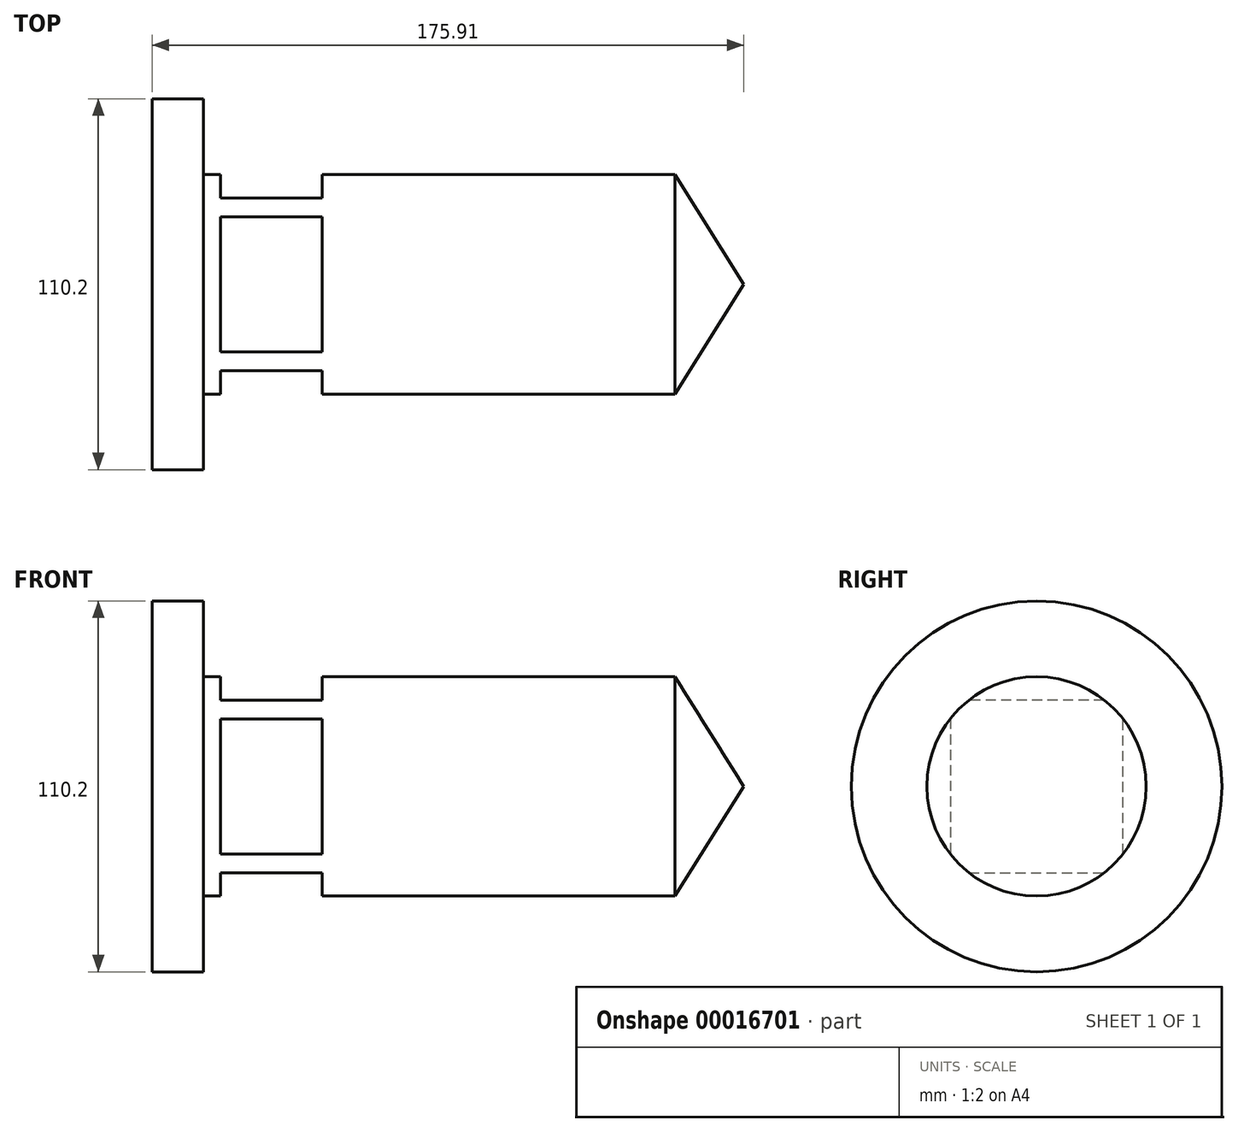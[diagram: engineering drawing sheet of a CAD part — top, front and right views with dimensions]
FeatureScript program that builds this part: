
annotation { "Feature Type Name" : "Feature", "Feature Type Description" : "" }
export const myFeature = defineFeature(function(context is Context, id is Id, definition is map)
    precondition{}
    {
        {
            var Q0;
            Q0=qCreatedBy(makeId("Front.planeOp"),FACE);
            var sketch = newSketch(context, id + "F0", { "sketchPlane" : qUnion([Q0])});
            skLineSegment(sketch, "E0", {"start": v(0, 0) * mm, "end": v(0, 55.1) * mm});
            skLineSegment(sketch, "E1", {"start": v(0, 55.1) * mm, "end": v(15.3, 55.1) * mm});
            skLineSegment(sketch, "E2", {"start": v(15.3, 55.1) * mm, "end": v(15.3, 32.6) * mm});
            skLineSegment(sketch, "E3", {"start": v(15.3, 32.6) * mm, "end": v(155.5, 32.6) * mm});
            skLineSegment(sketch, "E4", {"start": v(155.5, 32.6) * mm, "end": v(175.9, 0) * mm});
            skLineSegment(sketch, "E5", {"start": v(175.9, 0) * mm, "end": v(0, 0) * mm});
            skSolve(sketch);
        }
        {
            var Q0;
            Q0=makeQuery(id+"F0.imprint","IMPRINT",FACE,{"disambiguationData":[TD([[makeQuery(id+"F0.imprint","IMPRINT",EDGE,{"derivedFrom":sQuery(id+"F0.wireOp",EDGE,"E0")}),-1.0]])]});
            var Q1;
            Q1=sQuery(id+"F0.wireOp",EDGE,"E5");
            revolve(context, id + "F1", {"entities" : qUnion([Q0]), "axis" : qUnion([Q1]), "revolveType" : RevolveType.FULL});
        }
        {
            var Q0;
            Q0=qCreatedBy(makeId("Front.planeOp"),FACE);
            var sketch = newSketch(context, id + "F2", { "sketchPlane" : qUnion([Q0])});
            skLineSegment(sketch, "E6.bottom", {"start": v(20.37, 73.99) * mm, "end": v(50.6, 73.99) * mm});
            skLineSegment(sketch, "E6.top", {"start": v(20.37, 25.68) * mm, "end": v(50.6, 25.68) * mm});
            skLineSegment(sketch, "E6.left", {"start": v(20.37, 73.99) * mm, "end": v(20.37, 25.68) * mm});
            skLineSegment(sketch, "E6.right", {"start": v(50.6, 73.99) * mm, "end": v(50.6, 25.68) * mm});
            skSolve(sketch);
        }
        {
            var Q0;
            Q0 = qSketchRegion(id + "F2", true);
            extrude(context, id + "F3", {"entities" : qUnion([Q0]), "operationType" : NewBodyOperationType.REMOVE, "endBound" : BoundingType.SYMMETRIC, "oppositeDirection" : true, "depth" : 103.57 * mm});
        }
        {
            var Q0;
            Q0=makeQuery(id+"F3.boolean.opBoolean","COPY",FACE,{"derivedFrom":makeQuery(id+"F3.opExtrude","SWEPT_FACE",FACE,{"disambiguationData":[OSD([sQuery(id+"F2.wireOp",EDGE,"E6.top")])]})});
            var Q1;
            Q1=makeQuery(id+"F3.boolean.opBoolean","COPY",FACE,{"derivedFrom":makeQuery(id+"F3.opExtrude","SWEPT_FACE",FACE,{"disambiguationData":[OSD([sQuery(id+"F2.wireOp",EDGE,"E6.right")])]})});
            var Q2;
            Q2=makeQuery(id+"F3.boolean.opBoolean","COPY",FACE,{"derivedFrom":makeQuery(id+"F3.opExtrude","SWEPT_FACE",FACE,{"disambiguationData":[OSD([sQuery(id+"F2.wireOp",EDGE,"E6.left")])]})});
            var Q3;
            Q3=makeQuery(id+"F1.opRevolve","SWEPT_FACE",FACE,{"disambiguationData":[OSD([sQuery(id+"F0.wireOp",EDGE,"E3")])]});
            circularPattern(context, id + "F4", {"faces" : qUnion([Q0, Q1, Q2]), "axis" : qUnion([Q3]), "angle" : 360 * degree, "instanceCount" : 4, "equalSpace" : true, "patternType" : PatternType.FACE});
        }
    });
